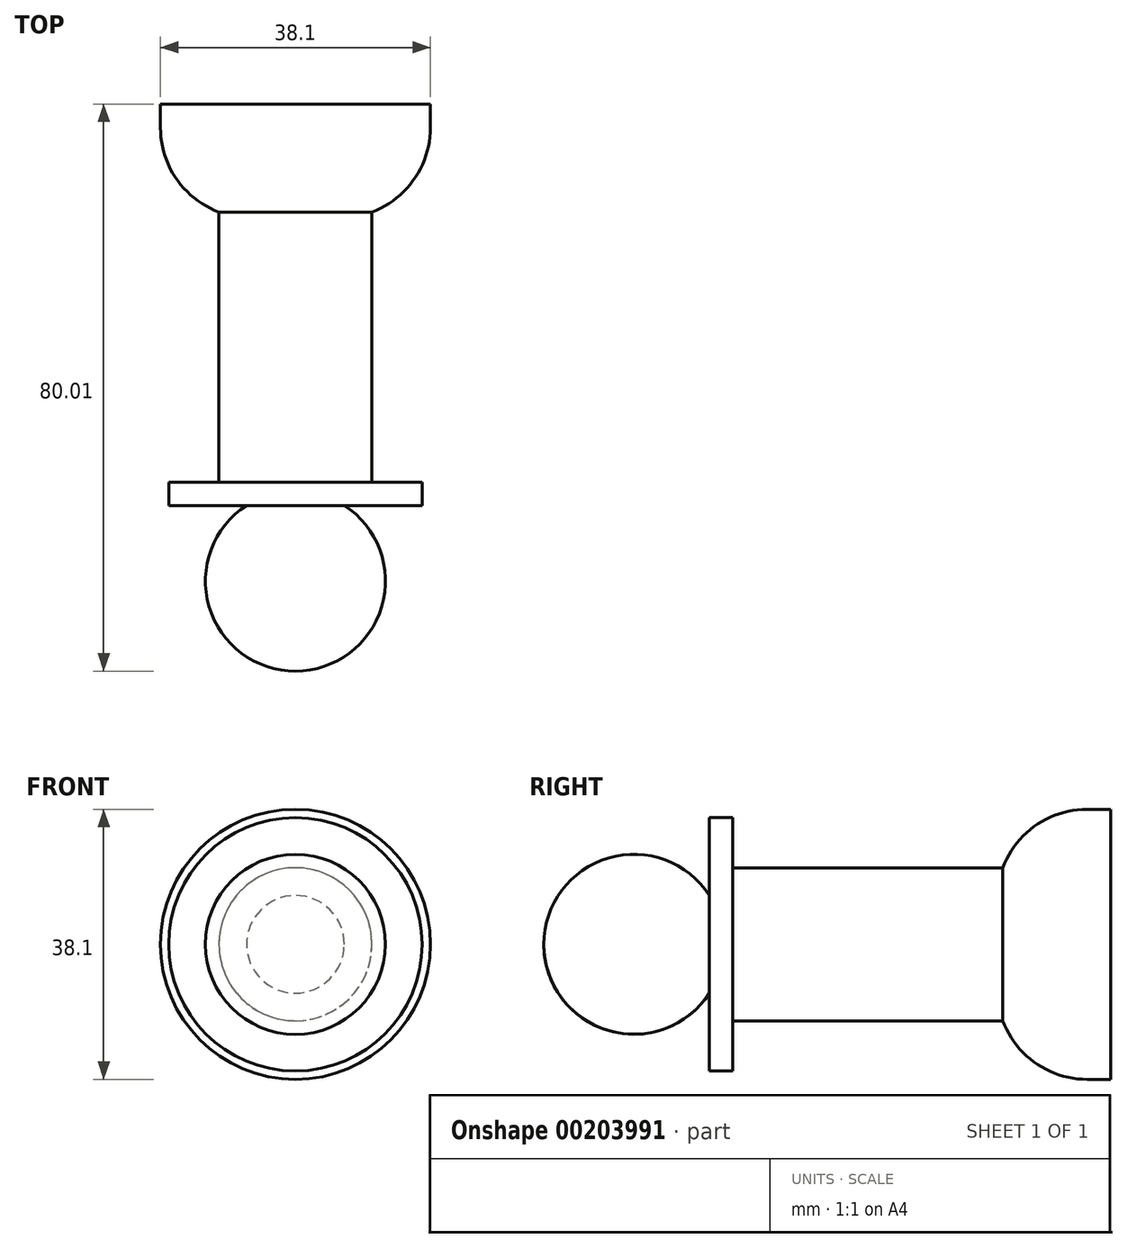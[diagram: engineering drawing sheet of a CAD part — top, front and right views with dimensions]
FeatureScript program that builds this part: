
annotation { "Feature Type Name" : "Feature", "Feature Type Description" : "" }
export const myFeature = defineFeature(function(context is Context, id is Id, definition is map)
    precondition{}
    {
        {
            var Q0;
            Q0=qCreatedBy(makeId("Front.planeOp"),FACE);
            var sketch = newSketch(context, id + "F0", { "sketchPlane" : qUnion([Q0])});
            skCircle(sketch, "E0", {"center": v(0, 0) * mm, "radius": 12.7 * mm});
            skSolve(sketch);
        }
        {
            var Q0;
            Q0=makeQuery(id+"F0.imprint","IMPRINT",FACE,{"disambiguationData":[TD([[makeQuery(id+"F0.imprint","IMPRINT",EDGE,{"derivedFrom":sQuery(id+"F0.wireOp",EDGE,"E0")}),1.0]])]});
            extrude(context, id + "F1", {"entities" : qUnion([Q0]), "depth" : 25.4 * mm});
        }
        {
            var Q0;
            Q0=makeQuery(id+"F1.opExtrude","CAP_EDGE",EDGE,{"disambiguationData":[OSD([sQuery(id+"F0.wireOp",EDGE,"E0")])],"isStart":false});
            fillet(context, id + "F2", {"entities" : qUnion([Q0]), "radius" : 12.7 * mm, "tangentPropagation" : true, "allowEdgeOverflow" : false});
        }
        {
            var Q0;
            Q0=makeQuery(id+"F1.opExtrude","CAP_EDGE",EDGE,{"disambiguationData":[OSD([sQuery(id+"F0.wireOp",EDGE,"E0")])],"isStart":true});
            fillet(context, id + "F3", {"entities" : qUnion([Q0]), "radius" : 12.7 * mm, "tangentPropagation" : true, "allowEdgeOverflow" : false});
        }
        {
            var Q0;
            Q0=qCreatedBy(makeId("Front.planeOp"),FACE);
            var sketch = newSketch(context, id + "F4", { "sketchPlane" : qUnion([Q0])});
            skCircle(sketch, "E1", {"center": v(0, 0) * mm, "radius": 17.88 * mm});
            skSolve(sketch);
        }
        {
            var Q0;
            Q0 = qSketchRegion(id + "F4", true);
            extrude(context, id + "F5", {"entities" : qUnion([Q0]), "operationType" : NewBodyOperationType.ADD, "oppositeDirection" : true, "depth" : 1.27 * mm, "hasSecondDirection" : true, "secondDirectionOppositeDirection" : false, "secondDirectionDepth" : 2.03 * mm});
        }
        {
            var Q0;
            Q0=makeQuery(id+"F5.opExtrude","CAP_FACE",FACE,{"disambiguationData":[OSD([sQuery(id+"F4.wireOp",EDGE,"E1")])],"isStart":false});
            var sketch = newSketch(context, id + "F6", { "sketchPlane" : qUnion([Q0])});
            skCircle(sketch, "E2", {"center": v(0, 0) * mm, "radius": 10.8 * mm});
            skSolve(sketch);
        }
        {
            var Q0;
            Q0 = qSketchRegion(id + "F6", true);
            extrude(context, id + "F7", {"entities" : qUnion([Q0]), "operationType" : NewBodyOperationType.ADD, "depth" : 38.1 * mm});
        }
        {
            var Q0;
            Q0=makeQuery(id+"F7.opExtrude","CAP_FACE",FACE,{"disambiguationData":[OSD([sQuery(id+"F6.wireOp",EDGE,"E2")])],"isStart":false});
            var sketch = newSketch(context, id + "F8", { "sketchPlane" : qUnion([Q0])});
            skCircle(sketch, "E3", {"center": v(0, 0) * mm, "radius": 19.05 * mm});
            skSolve(sketch);
        }
        {
            var Q0;
            Q0 = qSketchRegion(id + "F8", true);
            extrude(context, id + "F9", {"entities" : qUnion([Q0]), "operationType" : NewBodyOperationType.ADD, "depth" : 15.24 * mm});
        }
        {
            var Q0;
            Q0=makeQuery(id+"F9.opExtrude","CAP_EDGE",EDGE,{"disambiguationData":[OSD([sQuery(id+"F8.wireOp",EDGE,"E3")])],"isStart":true});
            fillet(context, id + "F10", {"entities" : qUnion([Q0]), "radius" : 12.7 * mm, "tangentPropagation" : true, "allowEdgeOverflow" : false});
        }
    });
